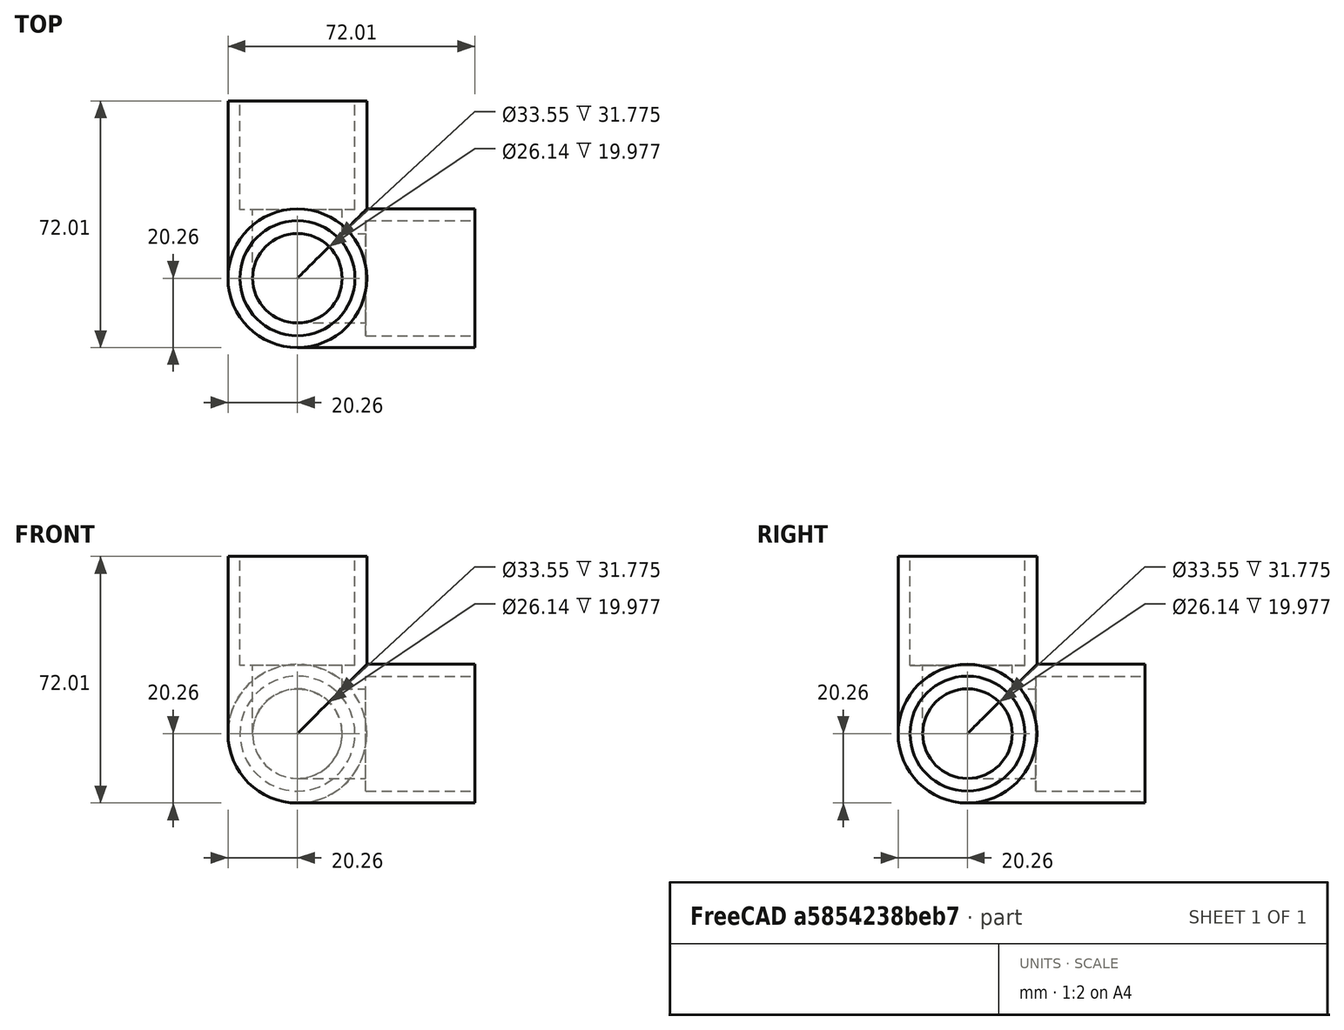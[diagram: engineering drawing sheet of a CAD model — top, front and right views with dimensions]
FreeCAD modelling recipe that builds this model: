
FCSTD DOCUMENT  (FreeCAD 0.17R13303 (Git))
Label: corner-test
License: All rights reserved
LicenseURL: http://en.wikipedia.org/wiki/All_rights_reserved
objects: Part::Cylinder×9, Part::Sphere×2, Part::MultiFuse×2, Part::Cut×1
note: 14 computed .brp shape members not serialized (recipe doc carries the construction recipe); baked Part::Feature solids carry a one-line shape summary decoded from their .brp

FEATURE [Part::Cylinder] XCynlider
  Angle = 360
  AttacherType = Attacher::AttachEngine3D
  Height = 51.7525
  Placement = pos=(0,0,0) rot=(0,1,0;1.5708rad)
  Radius = 20.2565
FEATURE [Part::Cylinder] YCynlider
  Angle = 360
  AttacherType = Attacher::AttachEngine3D
  Height = 51.7525
  Placement = pos=(0,0,0) rot=(1,0,0;-1.5708rad)
  Radius = 20.2565
FEATURE [Part::Cylinder] ZCynlider
  Angle = 360
  AttacherType = Attacher::AttachEngine3D
  Height = 51.7525
  Radius = 20.2565
FEATURE [Part::Sphere] Sphere
  Angle1 = -90
  Angle2 = 90
  Angle3 = 360
  AttacherType = Attacher::AttachEngine3D
  Radius = 20.2565
FEATURE [Part::MultiFuse] Fusion
  Shapes = -> [XCynlider,YCynlider,ZCynlider,Sphere]
FEATURE [Part::Cylinder] XCynlider001
  Angle = 360
  AttacherType = Attacher::AttachEngine3D
  Height = 51.7525
  Placement = pos=(0,0,0) rot=(0,1,0;1.5708rad)
  Radius = 13.0683
FEATURE [Part::Cylinder] YCynlider001
  Angle = 360
  AttacherType = Attacher::AttachEngine3D
  Height = 51.7525
  Placement = pos=(0,0,0) rot=(1,0,0;-1.5708rad)
  Radius = 13.0683
FEATURE [Part::Cylinder] ZCynlider001
  Angle = 360
  AttacherType = Attacher::AttachEngine3D
  Height = 51.7525
  Radius = 13.0683
FEATURE [Part::Sphere] Sphere001
  Angle1 = -90
  Angle2 = 90
  Angle3 = 360
  AttacherType = Attacher::AttachEngine3D
  Radius = 13.0683
FEATURE [Part::Cylinder] XSocket
  Angle = 360
  AttacherType = Attacher::AttachEngine3D
  Height = 31.7754
  Placement = pos=(19.9771,0,0) rot=(0,1,0;1.5708rad)
  Radius = 16.7767
FEATURE [Part::Cylinder] YSocket
  Angle = 360
  AttacherType = Attacher::AttachEngine3D
  Height = 31.7754
  Placement = pos=(0,19.9771,0) rot=(1,0,0;-1.5708rad)
  Radius = 16.7767
FEATURE [Part::Cylinder] ZSocket
  Angle = 360
  AttacherType = Attacher::AttachEngine3D
  Height = 31.7754
  Placement = pos=(0,0,19.9771) rot=(0,0,1;0rad)
  Radius = 16.7767
FEATURE [Part::MultiFuse] Fusion001
  Shapes = -> [XCynlider001,YCynlider001,ZCynlider001,Sphere001,XSocket,YSocket,ZSocket]
FEATURE [Part::Cut] Cut  label="F0013WE"
  Base = -> Fusion
  Tool = -> Fusion001
